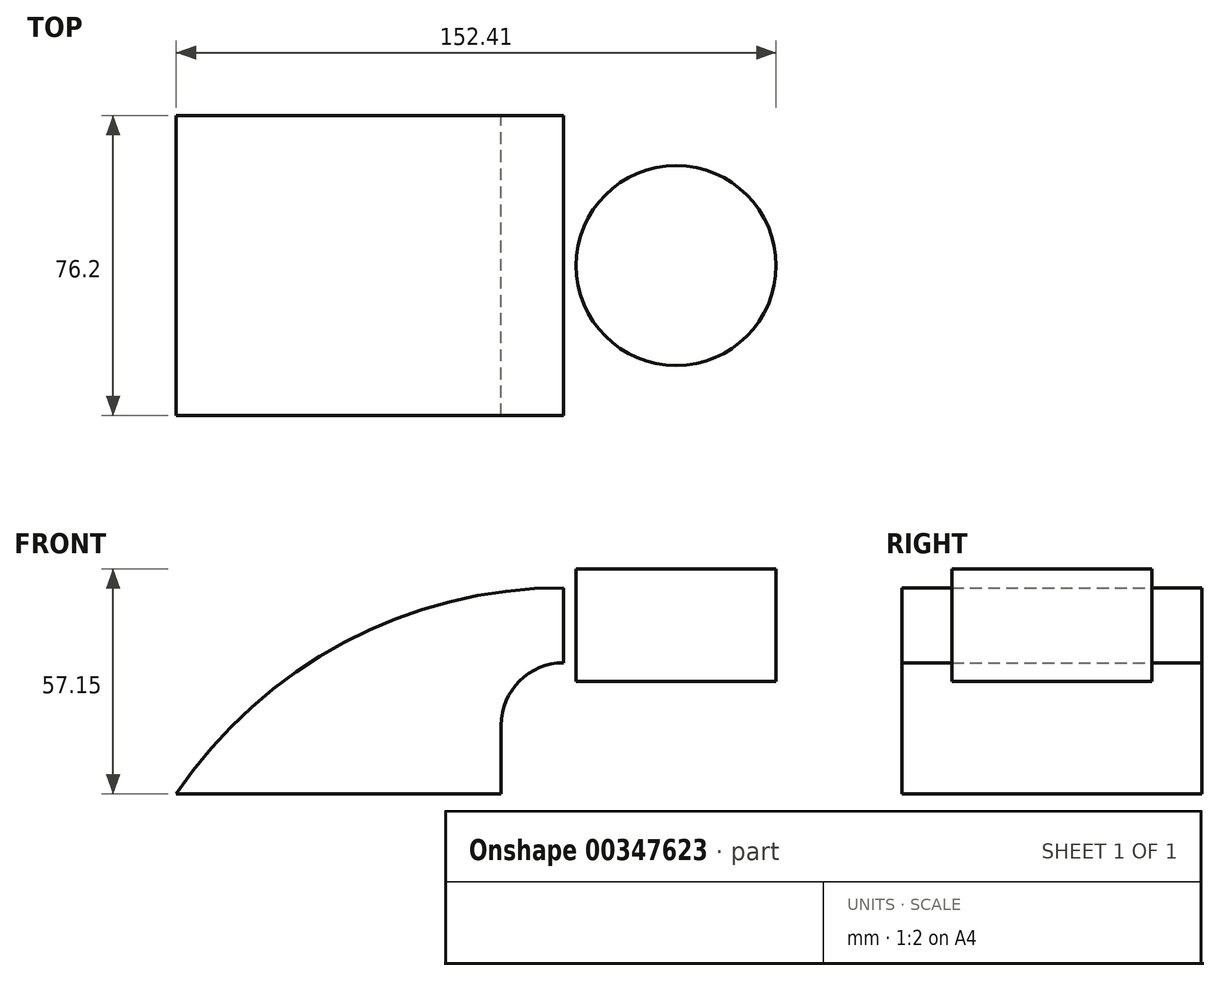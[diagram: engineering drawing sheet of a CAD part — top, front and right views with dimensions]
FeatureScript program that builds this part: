
annotation { "Feature Type Name" : "Feature", "Feature Type Description" : "" }
export const myFeature = defineFeature(function(context is Context, id is Id, definition is map)
    precondition{}
    {
        {
            var Q0;
            Q0=qCreatedBy(makeId("Front.planeOp"),FACE);
            var sketch = newSketch(context, id + "F0", { "sketchPlane" : qUnion([Q0])});
            skLineSegment(sketch, "E0.bottom", {"start": v(-41.27, -9.53) * mm, "end": v(41.28, -9.53) * mm});
            skLineSegment(sketch, "E0.top", {"start": v(-41.28, 9.52) * mm, "end": v(41.28, 9.52) * mm});
            skLineSegment(sketch, "E0.left", {"start": v(-41.28, -9.53) * mm, "end": v(-41.28, 9.53) * mm});
            skLineSegment(sketch, "E0.right", {"start": v(41.28, -9.53) * mm, "end": v(41.28, 9.52) * mm});
            skPoint(sketch, "E0.middle", {"position": v(0, 0) * mm});
            skLineSegment(sketch, "E1.bottom", {"start": v(111.12, 38.1) * mm, "end": v(60.33, 38.1) * mm});
            skLineSegment(sketch, "E1.top", {"start": v(111.12, 66.68) * mm, "end": v(60.33, 66.68) * mm});
            skLineSegment(sketch, "E1.left", {"start": v(111.12, 38.1) * mm, "end": v(111.12, 66.68) * mm});
            skLineSegment(sketch, "E1.right", {"start": v(60.33, 38.1) * mm, "end": v(60.33, 66.68) * mm});
            skPoint(sketch, "E1.middle", {"position": v(85.72, 52.39) * mm});
            skLineSegment(sketch, "E2", {"start": v(41.28, 9.52) * mm, "end": v(41.28, 27) * mm});
            skArc(sketch, "E3", {"start": v(57.15, 42.88) * mm, "mid": v(45.92, 38.23) * mm, "end": v(41.27, 27) * mm});
            skLineSegment(sketch, "E4", {"start": v(57.15, 42.88) * mm, "end": v(85.72, 42.88) * mm});
            skLineSegment(sketch, "E5", {"start": v(41.28, 9.52) * mm, "end": v(51.67, 9.52) * mm});
            skLineSegment(sketch, "E6", {"start": v(22.22, 9.53) * mm, "end": v(22.22, 27) * mm});
            skArc(sketch, "E7", {"start": v(57.15, 61.93) * mm, "mid": v(32.45, 51.7) * mm, "end": v(22.22, 27) * mm});
            skLineSegment(sketch, "E8", {"start": v(85.72, 52.39) * mm, "end": v(85.72, 66.68) * mm});
            skLineSegment(sketch, "E9", {"start": v(85.72, 66.68) * mm, "end": v(85.72, 38.1) * mm});
            skLineSegment(sketch, "E10", {"start": v(85.72, 38.1) * mm, "end": v(85.72, 61.93) * mm});
            skLineSegment(sketch, "E11", {"start": v(85.72, 61.93) * mm, "end": v(57.15, 61.93) * mm});
            skLineSegment(sketch, "E12", {"start": v(57.15, 61.93) * mm, "end": v(57.15, 42.88) * mm});
            skArc(sketch, "E13", {"start": v(57.15, 61.93) * mm, "mid": v(1.4, 48) * mm, "end": v(-41.27, 9.52) * mm});
            skSolve(sketch);
        }
        {
            var Q0;
            Q0=sQuery(id+"F0.wireOp",EDGE,"E0.bottom");
            var Q1;
            Q1=sQuery(id+"F0.wireOp",EDGE,"E0.top");
            var Q2;
            Q2=sQuery(id+"F0.wireOp",EDGE,"E0.left");
            var Q3;
            Q3=sQuery(id+"F0.wireOp",EDGE,"E0.right");
            extrude(context, id + "F1", {"bodyType" : ToolBodyType.SURFACE, "surfaceEntities" : qUnion([Q0, Q1, Q2, Q3]), "endBound" : BoundingType.SYMMETRIC, "depth" : 127 * mm});
        }
        {
            var Q0;
            {var subQ0=sQuery(id+"F0.wireOp",EDGE,"E2");Q0=makeQuery(id+"F0.imprint","IMPRINT",FACE,{"disambiguationData":[TD([[makeQuery(id+"F0.imprint","IMPRINT",EDGE,{"derivedFrom":subQ0}),1.0]])]});}
            var Q1;
            {var subQ2=sQuery(id+"F0.wireOp",EDGE,"E6");Q1=makeQuery(id+"F0.imprint","IMPRINT",FACE,{"disambiguationData":[TD([[makeQuery(id+"F0.imprint","IMPRINT",EDGE,{"derivedFrom":subQ2}),1.0]])]});}
            extrude(context, id + "F2", {"entities" : qUnion([Q0, Q1]), "endBound" : BoundingType.SYMMETRIC, "depth" : 76.2 * mm});
        }
        {
            var Q0;
            {var subQ1=sQuery(id+"F0.wireOp",EDGE,"E1.left");Q0=makeQuery(id+"F0.imprint","IMPRINT",FACE,{"disambiguationData":[TD([[makeQuery(id+"F0.imprint","IMPRINT",EDGE,{"derivedFrom":subQ1}),1.0]])]});}
            var Q1;
            Q1=sQuery(id+"F0.wireOp",EDGE,"E10");
            revolve(context, id + "F3", {"entities" : qUnion([Q0]), "axis" : qUnion([Q1]), "revolveType" : RevolveType.FULL});
        }
    });
